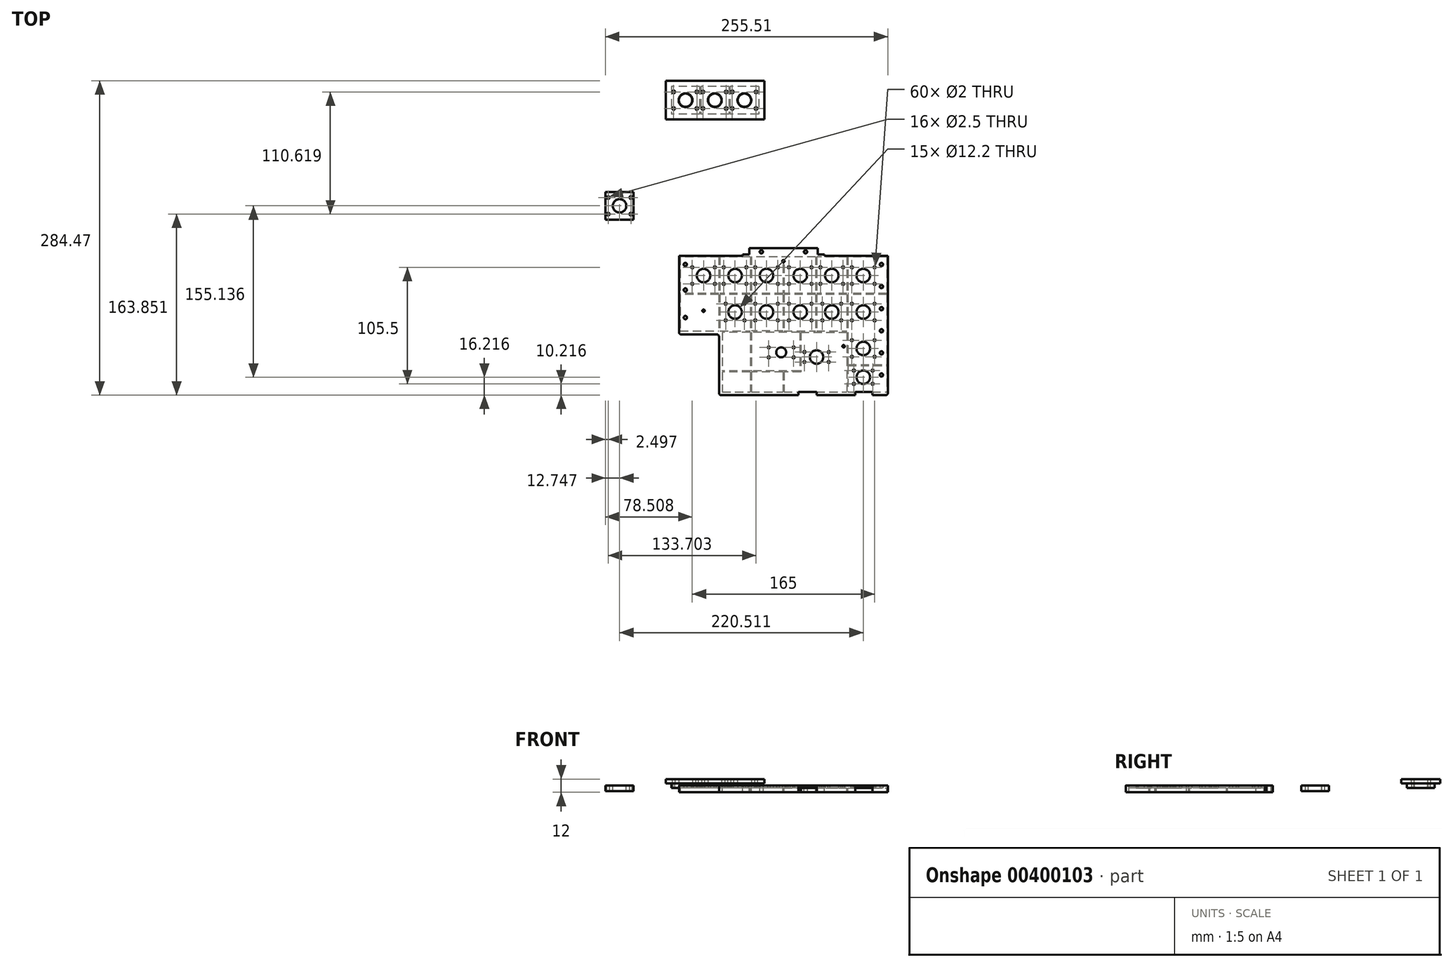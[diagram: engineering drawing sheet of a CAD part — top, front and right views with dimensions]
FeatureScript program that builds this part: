
annotation { "Feature Type Name" : "Feature", "Feature Type Description" : "" }
export const myFeature = defineFeature(function(context is Context, id is Id, definition is map)
    precondition{}
    {
        {
            var Q0;
            Q0=qCreatedBy(makeId("Top.planeOp"),FACE);
            var sketch = newSketch(context, id + "F0", { "sketchPlane" : qUnion([Q0])});
            skLineSegment(sketch, "E0.bottom", {"start": v(7.75, 12.5) * mm, "end": v(-7.75, 12.5) * mm});
            skLineSegment(sketch, "E0.top", {"start": v(7.75, -12.5) * mm, "end": v(-7.75, -12.5) * mm});
            skLineSegment(sketch, "E0.left", {"start": v(7.75, 12.5) * mm, "end": v(7.75, -12.5) * mm});
            skLineSegment(sketch, "E0.right", {"start": v(-7.75, 12.5) * mm, "end": v(-7.75, -12.5) * mm});
            skPoint(sketch, "E0.middle", {"position": v(0, 0) * mm});
            skLineSegment(sketch, "E1.bottom", {"start": v(-7.75, 12.5) * mm, "end": v(-12.75, 12.5) * mm});
            skLineSegment(sketch, "E1.top", {"start": v(-7.75, -12.5) * mm, "end": v(-12.75, -12.5) * mm});
            skLineSegment(sketch, "E1.right", {"start": v(-12.75, 12.5) * mm, "end": v(-12.75, -12.5) * mm});
            skLineSegment(sketch, "E2.bottom", {"start": v(7.75, 12.5) * mm, "end": v(12.75, 12.5) * mm});
            skLineSegment(sketch, "E2.top", {"start": v(7.75, -12.5) * mm, "end": v(12.75, -12.5) * mm});
            skLineSegment(sketch, "E2.right", {"start": v(12.75, 12.5) * mm, "end": v(12.75, -12.5) * mm});
            skCircle(sketch, "E3", {"center": v(-10.75, 7.5) * mm, "radius": 0.9 * mm});
            skPoint(sketch, "E3.centerSnap0", {"position": v(-10.25, 12.5) * mm});
            skCircle(sketch, "E4", {"center": v(-10.75, -7.5) * mm, "radius": 0.9 * mm});
            skCircle(sketch, "E5", {"center": v(10.25, 7.5) * mm, "radius": 0.9 * mm});
            skPoint(sketch, "E5.centerSnap0", {"position": v(10.25, 12.5) * mm});
            skCircle(sketch, "E6", {"center": v(10.25, -7.5) * mm, "radius": 0.9 * mm});
            skCircle(sketch, "E7", {"center": v(0, 0) * mm, "radius": 6 * mm});
            skLineSegment(sketch, "E8.bottom", {"start": v(34.25, 12.5) * mm, "end": v(18.75, 12.5) * mm});
            skLineSegment(sketch, "E8.top", {"start": v(34.25, -12.5) * mm, "end": v(18.75, -12.5) * mm});
            skLineSegment(sketch, "E8.left", {"start": v(34.25, 12.5) * mm, "end": v(34.25, -12.5) * mm});
            skLineSegment(sketch, "E8.right", {"start": v(18.75, 12.5) * mm, "end": v(18.75, -12.5) * mm});
            skPoint(sketch, "E8.middle", {"position": v(26.5, 0) * mm});
            skLineSegment(sketch, "E9.bottom", {"start": v(18.75, 12.5) * mm, "end": v(13.75, 12.5) * mm});
            skLineSegment(sketch, "E9.top", {"start": v(18.75, -12.5) * mm, "end": v(13.75, -12.5) * mm});
            skLineSegment(sketch, "E9.right", {"start": v(13.75, 12.5) * mm, "end": v(13.75, -12.5) * mm});
            skLineSegment(sketch, "E10.bottom", {"start": v(34.25, 12.5) * mm, "end": v(39.25, 12.5) * mm});
            skLineSegment(sketch, "E10.top", {"start": v(34.25, -12.5) * mm, "end": v(39.25, -12.5) * mm});
            skLineSegment(sketch, "E10.right", {"start": v(39.25, 12.5) * mm, "end": v(39.25, -12.5) * mm});
            skCircle(sketch, "E11", {"center": v(15.75, 7.5) * mm, "radius": 0.9 * mm});
            skPoint(sketch, "E11.centerSnap0", {"position": v(16.25, 12.5) * mm});
            skCircle(sketch, "E12", {"center": v(15.75, -7.5) * mm, "radius": 0.9 * mm});
            skCircle(sketch, "E13", {"center": v(36.75, 7.5) * mm, "radius": 0.9 * mm});
            skPoint(sketch, "E13.centerSnap0", {"position": v(36.75, 12.5) * mm});
            skCircle(sketch, "E14", {"center": v(36.75, -7.5) * mm, "radius": 0.9 * mm});
            skCircle(sketch, "E15", {"center": v(26.5, 0) * mm, "radius": 6 * mm});
            skLineSegment(sketch, "E16.bottom", {"start": v(61.25, 12.5) * mm, "end": v(45.25, 12.5) * mm});
            skLineSegment(sketch, "E16.top", {"start": v(61.25, -12.5) * mm, "end": v(45.25, -12.5) * mm});
            skLineSegment(sketch, "E16.left", {"start": v(61.25, 12.5) * mm, "end": v(61.25, -12.5) * mm});
            skLineSegment(sketch, "E16.right", {"start": v(45.25, 12.5) * mm, "end": v(45.25, -12.5) * mm});
            skPoint(sketch, "E16.middle", {"position": v(53.25, 0) * mm});
            skLineSegment(sketch, "E17.bottom", {"start": v(45.25, 12.5) * mm, "end": v(40.25, 12.5) * mm});
            skLineSegment(sketch, "E17.top", {"start": v(45.25, -12.5) * mm, "end": v(40.25, -12.5) * mm});
            skLineSegment(sketch, "E17.right", {"start": v(40.25, 12.5) * mm, "end": v(40.25, -12.5) * mm});
            skLineSegment(sketch, "E18.bottom", {"start": v(61.25, 12.5) * mm, "end": v(66.25, 12.5) * mm});
            skLineSegment(sketch, "E18.top", {"start": v(61.25, -12.5) * mm, "end": v(66.25, -12.5) * mm});
            skLineSegment(sketch, "E18.right", {"start": v(66.25, 12.5) * mm, "end": v(66.25, -12.5) * mm});
            skCircle(sketch, "E19", {"center": v(42.25, 7.5) * mm, "radius": 0.9 * mm});
            skPoint(sketch, "E19.centerSnap0", {"position": v(42.75, 12.5) * mm});
            skCircle(sketch, "E20", {"center": v(42.25, -7.5) * mm, "radius": 0.9 * mm});
            skCircle(sketch, "E21", {"center": v(63.75, 7.5) * mm, "radius": 0.9 * mm});
            skPoint(sketch, "E21.centerSnap0", {"position": v(63.75, 12.5) * mm});
            skCircle(sketch, "E22", {"center": v(63.75, -7.5) * mm, "radius": 0.9 * mm});
            skCircle(sketch, "E23", {"center": v(53.25, 0) * mm, "radius": 6 * mm});
            skSolve(sketch);
        }
        {
            var Q0;
            Q0=makeQuery(id+"F0.imprint","IMPRINT",FACE,{"disambiguationData":[TD([[makeQuery(id+"F0.imprint","IMPRINT",EDGE,{"derivedFrom":sQuery(id+"F0.wireOp",EDGE,"E0.bottom")}),1.0]])]});
            var Q1;
            Q1=makeQuery(id+"F0.imprint","IMPRINT",FACE,{"disambiguationData":[TD([[makeQuery(id+"F0.imprint","IMPRINT",EDGE,{"derivedFrom":sQuery(id+"F0.wireOp",EDGE,"E1.bottom")}),1.0]])]});
            var Q2;
            Q2=makeQuery(id+"F0.imprint","IMPRINT",FACE,{"disambiguationData":[TD([[makeQuery(id+"F0.imprint","IMPRINT",EDGE,{"derivedFrom":sQuery(id+"F0.wireOp",EDGE,"E2.bottom")}),-1.0]])]});
            var Q3;
            Q3=makeQuery(id+"F0.imprint","IMPRINT",FACE,{"disambiguationData":[TD([[makeQuery(id+"F0.imprint","IMPRINT",EDGE,{"derivedFrom":sQuery(id+"F0.wireOp",EDGE,"E9.bottom")}),1.0]])]});
            var Q4;
            Q4=makeQuery(id+"F0.imprint","IMPRINT",FACE,{"disambiguationData":[TD([[makeQuery(id+"F0.imprint","IMPRINT",EDGE,{"derivedFrom":sQuery(id+"F0.wireOp",EDGE,"E8.bottom")}),1.0]])]});
            var Q5;
            Q5=makeQuery(id+"F0.imprint","IMPRINT",FACE,{"disambiguationData":[TD([[makeQuery(id+"F0.imprint","IMPRINT",EDGE,{"derivedFrom":sQuery(id+"F0.wireOp",EDGE,"E10.bottom")}),-1.0]])]});
            var Q6;
            Q6=makeQuery(id+"F0.imprint","IMPRINT",FACE,{"disambiguationData":[TD([[makeQuery(id+"F0.imprint","IMPRINT",EDGE,{"derivedFrom":sQuery(id+"F0.wireOp",EDGE,"E17.bottom")}),1.0]])]});
            var Q7;
            Q7=makeQuery(id+"F0.imprint","IMPRINT",FACE,{"disambiguationData":[TD([[makeQuery(id+"F0.imprint","IMPRINT",EDGE,{"derivedFrom":sQuery(id+"F0.wireOp",EDGE,"E16.bottom")}),1.0]])]});
            var Q8;
            Q8=makeQuery(id+"F0.imprint","IMPRINT",FACE,{"disambiguationData":[TD([[makeQuery(id+"F0.imprint","IMPRINT",EDGE,{"derivedFrom":sQuery(id+"F0.wireOp",EDGE,"E18.bottom")}),-1.0]])]});
            extrude(context, id + "F1", {"entities" : qUnion([Q0, Q1, Q2, Q3, Q4, Q5, Q6, Q7, Q8]), "depth" : 4 * mm});
        }
        {
            var Q0;
            Q0=makeQuery(id+"F1.opExtrude","CAP_FACE",FACE,{"disambiguationData":[OSD([sQuery(id+"F0.wireOp",EDGE,"E0.bottom"),sQuery(id+"F0.wireOp",EDGE,"E0.top"),sQuery(id+"F0.wireOp",EDGE,"E1.bottom"),sQuery(id+"F0.wireOp",EDGE,"E1.top"),sQuery(id+"F0.wireOp",EDGE,"E1.right"),sQuery(id+"F0.wireOp",EDGE,"E2.bottom"),sQuery(id+"F0.wireOp",EDGE,"E2.top"),sQuery(id+"F0.wireOp",EDGE,"E2.right"),sQuery(id+"F0.wireOp",EDGE,"E3"),sQuery(id+"F0.wireOp",EDGE,"E4"),sQuery(id+"F0.wireOp",EDGE,"E5"),sQuery(id+"F0.wireOp",EDGE,"E6"),sQuery(id+"F0.wireOp",EDGE,"E7")])],"isStart":false});
            var sketch = newSketch(context, id + "F2", { "sketchPlane" : qUnion([Q0])});
            skLineSegment(sketch, "E24.bottom", {"start": v(-17.75, 17.5) * mm, "end": v(71.25, 17.5) * mm});
            skLineSegment(sketch, "E24.top", {"start": v(-17.75, -17.5) * mm, "end": v(71.25, -17.5) * mm});
            skLineSegment(sketch, "E24.left", {"start": v(-17.75, 17.5) * mm, "end": v(-17.75, -17.5) * mm});
            skLineSegment(sketch, "E24.right", {"start": v(71.25, 17.5) * mm, "end": v(71.25, -17.5) * mm});
            skCircle(sketch, "E25", {"center": v(-10.75, 7.5) * mm, "radius": 1.25 * mm});
            skCircle(sketch, "E26", {"center": v(-10.75, -7.5) * mm, "radius": 1.25 * mm});
            skCircle(sketch, "E27", {"center": v(10.25, -7.5) * mm, "radius": 1.25 * mm});
            skCircle(sketch, "E28", {"center": v(10.25, 7.5) * mm, "radius": 1.25 * mm});
            skCircle(sketch, "E29", {"center": v(15.75, 7.5) * mm, "radius": 1.25 * mm});
            skCircle(sketch, "E30", {"center": v(15.75, -7.5) * mm, "radius": 1.25 * mm});
            skCircle(sketch, "E31", {"center": v(36.75, -7.5) * mm, "radius": 1.25 * mm});
            skCircle(sketch, "E32", {"center": v(0, 0) * mm, "radius": 6.25 * mm});
            skCircle(sketch, "E33", {"center": v(26.5, 0) * mm, "radius": 6.25 * mm});
            skCircle(sketch, "E34", {"center": v(53.25, 0) * mm, "radius": 6.25 * mm});
            skCircle(sketch, "E35", {"center": v(36.75, 7.5) * mm, "radius": 1.25 * mm});
            skCircle(sketch, "E36", {"center": v(42.25, 7.5) * mm, "radius": 1.25 * mm});
            skCircle(sketch, "E37", {"center": v(42.25, -7.5) * mm, "radius": 1.25 * mm});
            skCircle(sketch, "E38", {"center": v(63.75, 7.5) * mm, "radius": 1.25 * mm});
            skCircle(sketch, "E39", {"center": v(63.75, -7.5) * mm, "radius": 1.25 * mm});
            skSolve(sketch);
        }
        {
            var Q0;
            Q0=qSketchRegion(id+"F2",true);
            extrude(context, id + "F3", {"entities" : qUnion([Q0]), "depth" : 4 * mm});
        }
        {
            var Q0;
            Q0=qCreatedBy(makeId("Top.planeOp"),FACE);
            var sketch = newSketch(context, id + "F4", { "sketchPlane" : qUnion([Q0])});
            skLineSegment(sketch, "E40.bottom", {"start": v(3.56, -143.75) * mm, "end": v(29.06, -143.75) * mm, "construction": true});
            skLineSegment(sketch, "E40.top", {"start": v(3.56, -173.75) * mm, "end": v(29.06, -173.75) * mm, "construction": true});
            skLineSegment(sketch, "E40.left", {"start": v(3.56, -143.75) * mm, "end": v(3.56, -173.75) * mm, "construction": true});
            skLineSegment(sketch, "E40.right", {"start": v(29.06, -143.75) * mm, "end": v(29.06, -173.75) * mm, "construction": true});
            skLineSegment(sketch, "E41.bottom", {"start": v(32.06, -143.75) * mm, "end": v(57.56, -143.75) * mm, "construction": true});
            skLineSegment(sketch, "E41.top", {"start": v(32.06, -173.75) * mm, "end": v(57.56, -173.75) * mm, "construction": true});
            skLineSegment(sketch, "E41.left", {"start": v(32.06, -143.75) * mm, "end": v(32.06, -173.75) * mm, "construction": true});
            skLineSegment(sketch, "E41.right", {"start": v(57.56, -143.75) * mm, "end": v(57.56, -173.75) * mm, "construction": true});
            skLineSegment(sketch, "E42.bottom", {"start": v(60.56, -143.75) * mm, "end": v(86.06, -143.75) * mm, "construction": true});
            skLineSegment(sketch, "E42.top", {"start": v(60.56, -173.75) * mm, "end": v(86.06, -173.75) * mm, "construction": true});
            skLineSegment(sketch, "E42.left", {"start": v(60.56, -143.75) * mm, "end": v(60.56, -173.75) * mm, "construction": true});
            skLineSegment(sketch, "E42.right", {"start": v(86.06, -143.75) * mm, "end": v(86.06, -173.75) * mm, "construction": true});
            skLineSegment(sketch, "E43.bottom", {"start": v(91.06, -143.75) * mm, "end": v(116.56, -143.75) * mm, "construction": true});
            skLineSegment(sketch, "E43.top", {"start": v(91.06, -173.75) * mm, "end": v(116.56, -173.75) * mm, "construction": true});
            skLineSegment(sketch, "E43.left", {"start": v(91.06, -143.75) * mm, "end": v(91.06, -173.75) * mm, "construction": true});
            skLineSegment(sketch, "E43.right", {"start": v(116.56, -143.75) * mm, "end": v(116.56, -173.75) * mm, "construction": true});
            skLineSegment(sketch, "E44.bottom", {"start": v(119.56, -143.75) * mm, "end": v(145.06, -143.75) * mm, "construction": true});
            skLineSegment(sketch, "E44.top", {"start": v(119.56, -173.75) * mm, "end": v(145.06, -173.75) * mm, "construction": true});
            skLineSegment(sketch, "E44.left", {"start": v(119.56, -143.75) * mm, "end": v(119.56, -173.75) * mm, "construction": true});
            skLineSegment(sketch, "E44.right", {"start": v(145.06, -143.75) * mm, "end": v(145.06, -173.75) * mm, "construction": true});
            skLineSegment(sketch, "E45.bottom", {"start": v(148.06, -143.75) * mm, "end": v(173.56, -143.75) * mm, "construction": true});
            skLineSegment(sketch, "E45.top", {"start": v(148.06, -173.75) * mm, "end": v(173.56, -173.75) * mm, "construction": true});
            skLineSegment(sketch, "E45.left", {"start": v(148.06, -143.75) * mm, "end": v(148.06, -173.75) * mm, "construction": true});
            skLineSegment(sketch, "E45.right", {"start": v(173.56, -143.75) * mm, "end": v(173.56, -173.75) * mm, "construction": true});
            skLineSegment(sketch, "E46.bottom", {"start": v(60.56, -176.75) * mm, "end": v(86.06, -176.75) * mm, "construction": true});
            skLineSegment(sketch, "E46.top", {"start": v(60.56, -206.75) * mm, "end": v(86.06, -206.75) * mm, "construction": true});
            skLineSegment(sketch, "E46.left", {"start": v(60.56, -176.75) * mm, "end": v(60.56, -206.75) * mm, "construction": true});
            skLineSegment(sketch, "E46.right", {"start": v(86.06, -176.75) * mm, "end": v(86.06, -206.75) * mm, "construction": true});
            skLineSegment(sketch, "E47.bottom", {"start": v(91.06, -176.75) * mm, "end": v(116.56, -176.75) * mm, "construction": true});
            skLineSegment(sketch, "E47.top", {"start": v(91.06, -206.75) * mm, "end": v(116.56, -206.75) * mm, "construction": true});
            skLineSegment(sketch, "E47.left", {"start": v(91.06, -176.75) * mm, "end": v(91.06, -206.75) * mm, "construction": true});
            skLineSegment(sketch, "E47.right", {"start": v(116.56, -176.75) * mm, "end": v(116.56, -206.75) * mm, "construction": true});
            skLineSegment(sketch, "E48.bottom", {"start": v(148.06, -176.75) * mm, "end": v(173.56, -176.75) * mm, "construction": true});
            skLineSegment(sketch, "E48.top", {"start": v(148.06, -206.75) * mm, "end": v(173.56, -206.75) * mm, "construction": true});
            skLineSegment(sketch, "E48.left", {"start": v(148.06, -176.75) * mm, "end": v(148.06, -206.75) * mm, "construction": true});
            skLineSegment(sketch, "E48.right", {"start": v(173.56, -176.75) * mm, "end": v(173.56, -206.75) * mm, "construction": true});
            skLineSegment(sketch, "E49.bottom", {"start": v(148.06, -208.75) * mm, "end": v(173.56, -208.75) * mm, "construction": true});
            skLineSegment(sketch, "E49.top", {"start": v(148.06, -238.75) * mm, "end": v(173.56, -238.75) * mm, "construction": true});
            skLineSegment(sketch, "E49.left", {"start": v(148.06, -208.75) * mm, "end": v(148.06, -238.75) * mm, "construction": true});
            skLineSegment(sketch, "E49.right", {"start": v(173.56, -208.75) * mm, "end": v(173.56, -238.75) * mm, "construction": true});
            skLineSegment(sketch, "E50.bottom", {"start": v(-4.94, -140.75) * mm, "end": v(182.06, -140.75) * mm});
            skLineSegment(sketch, "E50.top", {"start": v(33.28, -263.97) * mm, "end": v(182.06, -263.97) * mm});
            skLineSegment(sketch, "E50.left", {"start": v(-4.94, -140.75) * mm, "end": v(-4.94, -208.97) * mm});
            skLineSegment(sketch, "E50.right", {"start": v(182.06, -140.75) * mm, "end": v(182.06, -263.97) * mm});
            skLineSegment(sketch, "E51", {"start": v(-4.94, -208.97) * mm, "end": v(33.28, -208.97) * mm});
            skLineSegment(sketch, "E52", {"start": v(33.28, -208.97) * mm, "end": v(33.28, -263.97) * mm});
            skLineSegment(sketch, "E53.bottom", {"start": v(-67.45, -83.12) * mm, "end": v(-51.95, -83.12) * mm});
            skLineSegment(sketch, "E53.top", {"start": v(-67.45, -108.12) * mm, "end": v(-51.95, -108.12) * mm});
            skLineSegment(sketch, "E53.left", {"start": v(-67.45, -83.12) * mm, "end": v(-67.45, -108.12) * mm});
            skLineSegment(sketch, "E53.right", {"start": v(-51.95, -83.12) * mm, "end": v(-51.95, -108.12) * mm});
            skLineSegment(sketch, "E54.bottom", {"start": v(-51.95, -83.12) * mm, "end": v(-46.95, -83.12) * mm});
            skLineSegment(sketch, "E54.top", {"start": v(-51.95, -108.12) * mm, "end": v(-46.95, -108.12) * mm});
            skLineSegment(sketch, "E54.right", {"start": v(-46.95, -83.12) * mm, "end": v(-46.95, -108.12) * mm});
            skLineSegment(sketch, "E55.bottom", {"start": v(-67.45, -83.12) * mm, "end": v(-72.45, -83.12) * mm});
            skLineSegment(sketch, "E55.top", {"start": v(-67.45, -108.12) * mm, "end": v(-72.45, -108.12) * mm});
            skLineSegment(sketch, "E55.right", {"start": v(-72.45, -83.12) * mm, "end": v(-72.45, -108.12) * mm});
            skCircle(sketch, "E56", {"center": v(-59.7, -95.62) * mm, "radius": 6.1 * mm});
            skPoint(sketch, "E56.centerSnap0", {"position": v(-67.45, -95.62) * mm});
            skPoint(sketch, "E56.centerSnap1", {"position": v(-59.7, -83.12) * mm});
            skCircle(sketch, "E57", {"center": v(-69.95, -88.12) * mm, "radius": 1.25 * mm});
            skPoint(sketch, "E57.centerSnap0", {"position": v(-69.95, -83.12) * mm});
            skCircle(sketch, "E58", {"center": v(-69.95, -103.12) * mm, "radius": 1.25 * mm});
            skCircle(sketch, "E59", {"center": v(-49.45, -88.12) * mm, "radius": 1.25 * mm});
            skPoint(sketch, "E59.centerSnap0", {"position": v(-49.45, -83.12) * mm});
            skCircle(sketch, "E60", {"center": v(-49.45, -103.12) * mm, "radius": 1.25 * mm});
            skLineSegment(sketch, "E61.bottom", {"start": v(33.8, -180.75) * mm, "end": v(55.8, -180.75) * mm, "construction": true});
            skLineSegment(sketch, "E61.top", {"start": v(33.8, -202.75) * mm, "end": v(55.8, -202.75) * mm, "construction": true});
            skLineSegment(sketch, "E61.left", {"start": v(33.8, -180.75) * mm, "end": v(33.8, -202.75) * mm, "construction": true});
            skLineSegment(sketch, "E61.right", {"start": v(55.8, -180.75) * mm, "end": v(55.8, -202.75) * mm, "construction": true});
            skLineSegment(sketch, "E62.bottom", {"start": v(121.3, -180.75) * mm, "end": v(143.3, -180.75) * mm, "construction": true});
            skLineSegment(sketch, "E62.top", {"start": v(121.3, -202.75) * mm, "end": v(143.3, -202.75) * mm, "construction": true});
            skLineSegment(sketch, "E62.left", {"start": v(121.3, -180.75) * mm, "end": v(121.3, -202.75) * mm, "construction": true});
            skLineSegment(sketch, "E62.right", {"start": v(143.3, -180.75) * mm, "end": v(143.3, -202.75) * mm, "construction": true});
            skLineSegment(sketch, "E63.bottom", {"start": v(105.06, -224.97) * mm, "end": v(111.06, -224.97) * mm, "construction": true});
            skLineSegment(sketch, "E63.top", {"start": v(105.06, -239.97) * mm, "end": v(110.06, -239.97) * mm, "construction": true});
            skLineSegment(sketch, "E63.left", {"start": v(105.06, -224.97) * mm, "end": v(105.06, -239.97) * mm, "construction": true});
            skLineSegment(sketch, "E64.bottom", {"start": v(132.06, -224.97) * mm, "end": v(126.06, -224.97) * mm, "construction": true});
            skLineSegment(sketch, "E64.top", {"start": v(132.06, -239.97) * mm, "end": v(126.06, -239.97) * mm, "construction": true});
            skLineSegment(sketch, "E64.left", {"start": v(132.06, -224.97) * mm, "end": v(132.06, -239.97) * mm, "construction": true});
            skLineSegment(sketch, "E64.right", {"start": v(126.06, -224.97) * mm, "end": v(126.06, -239.97) * mm, "construction": true});
            skLineSegment(sketch, "E65.bottom", {"start": v(3.56, -146.25) * mm, "end": v(8.56, -146.25) * mm, "construction": true});
            skLineSegment(sketch, "E65.top", {"start": v(3.56, -171.25) * mm, "end": v(8.56, -171.25) * mm, "construction": true});
            skLineSegment(sketch, "E65.left", {"start": v(3.56, -146.25) * mm, "end": v(3.56, -171.25) * mm, "construction": true});
            skLineSegment(sketch, "E65.right", {"start": v(8.56, -146.25) * mm, "end": v(8.56, -171.25) * mm, "construction": true});
            skLineSegment(sketch, "E66.bottom", {"start": v(29.06, -146.25) * mm, "end": v(24.06, -146.25) * mm, "construction": true});
            skLineSegment(sketch, "E66.top", {"start": v(29.06, -171.25) * mm, "end": v(24.06, -171.25) * mm, "construction": true});
            skLineSegment(sketch, "E66.left", {"start": v(29.06, -146.25) * mm, "end": v(29.06, -171.25) * mm, "construction": true});
            skLineSegment(sketch, "E66.right", {"start": v(24.06, -146.25) * mm, "end": v(24.06, -171.25) * mm, "construction": true});
            skCircle(sketch, "E67", {"center": v(6.06, -151.25) * mm, "radius": 1 * mm});
            skPoint(sketch, "E67.centerSnap0", {"position": v(6.06, -146.25) * mm});
            skCircle(sketch, "E68", {"center": v(6.06, -166.25) * mm, "radius": 1 * mm});
            skCircle(sketch, "E69", {"center": v(16.3, -158.75) * mm, "radius": 6.1 * mm});
            skPoint(sketch, "E69.centerSnap0", {"position": v(8.56, -158.75) * mm});
            skPoint(sketch, "E69.centerSnap1", {"position": v(16.3, -143.75) * mm});
            skCircle(sketch, "E70", {"center": v(26.56, -151.25) * mm, "radius": 1 * mm});
            skPoint(sketch, "E70.centerSnap0", {"position": v(26.56, -146.25) * mm});
            skCircle(sketch, "E71", {"center": v(26.56, -166.25) * mm, "radius": 1 * mm});
            skCircle(sketch, "E72", {"center": v(107.56, -227.97) * mm, "radius": 1 * mm});
            skPoint(sketch, "E72.centerSnap0", {"position": v(108.06, -224.97) * mm});
            skCircle(sketch, "E73", {"center": v(107.56, -236.97) * mm, "radius": 1 * mm});
            skPoint(sketch, "E73.centerSnap0", {"position": v(107.56, -239.97) * mm});
            skCircle(sketch, "E74", {"center": v(129.56, -227.97) * mm, "radius": 1 * mm});
            skPoint(sketch, "E74.centerSnap0", {"position": v(129.06, -224.97) * mm});
            skCircle(sketch, "E75", {"center": v(129.56, -236.97) * mm, "radius": 1 * mm});
            skPoint(sketch, "E75.centerSnap0", {"position": v(129.06, -239.97) * mm});
            skPoint(sketch, "E76.centerSnap0", {"position": v(110.56, -232.47) * mm});
            skLineSegment(sketch, "E77.bottom", {"start": v(38.8, -185.75) * mm, "end": v(50.8, -185.75) * mm, "construction": true});
            skLineSegment(sketch, "E77.top", {"start": v(38.8, -197.75) * mm, "end": v(50.8, -197.75) * mm, "construction": true});
            skLineSegment(sketch, "E77.left", {"start": v(38.8, -185.75) * mm, "end": v(38.8, -197.75) * mm, "construction": true});
            skLineSegment(sketch, "E77.right", {"start": v(50.8, -185.75) * mm, "end": v(50.8, -197.75) * mm, "construction": true});
            skLineSegment(sketch, "E78.bottom", {"start": v(149.8, -239.75) * mm, "end": v(171.8, -239.75) * mm, "construction": true});
            skLineSegment(sketch, "E78.top", {"start": v(149.8, -261.75) * mm, "end": v(171.8, -261.75) * mm, "construction": true});
            skLineSegment(sketch, "E78.left", {"start": v(149.8, -239.75) * mm, "end": v(149.8, -261.75) * mm, "construction": true});
            skLineSegment(sketch, "E78.right", {"start": v(171.8, -239.75) * mm, "end": v(171.8, -261.75) * mm, "construction": true});
            skLineSegment(sketch, "E79.bottom", {"start": v(154.8, -244.75) * mm, "end": v(166.8, -244.75) * mm, "construction": true});
            skLineSegment(sketch, "E79.top", {"start": v(154.8, -256.75) * mm, "end": v(166.8, -256.75) * mm, "construction": true});
            skLineSegment(sketch, "E79.left", {"start": v(154.8, -244.75) * mm, "end": v(154.8, -256.75) * mm, "construction": true});
            skLineSegment(sketch, "E79.right", {"start": v(166.8, -244.75) * mm, "end": v(166.8, -256.75) * mm, "construction": true});
            skLineSegment(sketch, "E80.bottom", {"start": v(77.8, -218.75) * mm, "end": v(95.3, -218.75) * mm, "construction": true});
            skLineSegment(sketch, "E80.top", {"start": v(77.8, -237.75) * mm, "end": v(95.3, -237.75) * mm, "construction": true});
            skLineSegment(sketch, "E80.left", {"start": v(77.8, -218.75) * mm, "end": v(77.8, -237.75) * mm, "construction": true});
            skLineSegment(sketch, "E80.right", {"start": v(95.3, -218.75) * mm, "end": v(95.3, -237.75) * mm, "construction": true});
            skLineSegment(sketch, "E81.bottom", {"start": v(32.06, -146.25) * mm, "end": v(37.06, -146.25) * mm, "construction": true});
            skLineSegment(sketch, "E81.top", {"start": v(32.06, -171.25) * mm, "end": v(37.06, -171.25) * mm, "construction": true});
            skLineSegment(sketch, "E81.left", {"start": v(32.06, -146.25) * mm, "end": v(32.06, -171.25) * mm, "construction": true});
            skLineSegment(sketch, "E81.right", {"start": v(37.06, -146.25) * mm, "end": v(37.06, -171.25) * mm, "construction": true});
            skLineSegment(sketch, "E82.bottom", {"start": v(57.56, -146.25) * mm, "end": v(52.56, -146.25) * mm, "construction": true});
            skLineSegment(sketch, "E82.top", {"start": v(57.56, -171.25) * mm, "end": v(52.56, -171.25) * mm, "construction": true});
            skLineSegment(sketch, "E82.left", {"start": v(57.56, -146.25) * mm, "end": v(57.56, -171.25) * mm, "construction": true});
            skLineSegment(sketch, "E82.right", {"start": v(52.56, -146.25) * mm, "end": v(52.56, -171.25) * mm, "construction": true});
            skCircle(sketch, "E83", {"center": v(34.56, -151.25) * mm, "radius": 1 * mm});
            skPoint(sketch, "E83.centerSnap0", {"position": v(34.56, -146.25) * mm});
            skCircle(sketch, "E84", {"center": v(34.56, -166.25) * mm, "radius": 1 * mm});
            skCircle(sketch, "E85", {"center": v(55.06, -151.25) * mm, "radius": 1 * mm});
            skPoint(sketch, "E85.centerSnap0", {"position": v(55.06, -146.25) * mm});
            skCircle(sketch, "E86", {"center": v(55.06, -166.25) * mm, "radius": 1 * mm});
            skCircle(sketch, "E87", {"center": v(44.8, -158.75) * mm, "radius": 6.1 * mm});
            skPoint(sketch, "E87.centerSnap0", {"position": v(37.06, -158.75) * mm});
            skPoint(sketch, "E87.centerSnap1", {"position": v(44.8, -143.75) * mm});
            skLineSegment(sketch, "E88.bottom", {"start": v(60.56, -146.25) * mm, "end": v(65.56, -146.25) * mm, "construction": true});
            skLineSegment(sketch, "E88.top", {"start": v(60.56, -171.25) * mm, "end": v(65.56, -171.25) * mm, "construction": true});
            skLineSegment(sketch, "E88.left", {"start": v(60.56, -146.25) * mm, "end": v(60.56, -171.25) * mm, "construction": true});
            skLineSegment(sketch, "E88.right", {"start": v(65.56, -146.25) * mm, "end": v(65.56, -171.25) * mm, "construction": true});
            skLineSegment(sketch, "E89.bottom", {"start": v(86.06, -146.25) * mm, "end": v(81.06, -146.25) * mm, "construction": true});
            skLineSegment(sketch, "E89.top", {"start": v(86.06, -171.25) * mm, "end": v(81.06, -171.25) * mm, "construction": true});
            skLineSegment(sketch, "E89.left", {"start": v(86.06, -146.25) * mm, "end": v(86.06, -171.25) * mm, "construction": true});
            skLineSegment(sketch, "E89.right", {"start": v(81.06, -146.25) * mm, "end": v(81.06, -171.25) * mm, "construction": true});
            skLineSegment(sketch, "E90.bottom", {"start": v(91.06, -146.25) * mm, "end": v(96.06, -146.25) * mm, "construction": true});
            skLineSegment(sketch, "E90.top", {"start": v(91.06, -171.25) * mm, "end": v(96.06, -171.25) * mm, "construction": true});
            skLineSegment(sketch, "E90.left", {"start": v(91.06, -146.25) * mm, "end": v(91.06, -171.25) * mm, "construction": true});
            skLineSegment(sketch, "E90.right", {"start": v(96.06, -146.25) * mm, "end": v(96.06, -171.25) * mm, "construction": true});
            skLineSegment(sketch, "E91.bottom", {"start": v(116.56, -146.25) * mm, "end": v(111.56, -146.25) * mm, "construction": true});
            skLineSegment(sketch, "E91.top", {"start": v(116.56, -171.25) * mm, "end": v(111.56, -171.25) * mm, "construction": true});
            skLineSegment(sketch, "E91.left", {"start": v(116.56, -146.25) * mm, "end": v(116.56, -171.25) * mm, "construction": true});
            skLineSegment(sketch, "E91.right", {"start": v(111.56, -146.25) * mm, "end": v(111.56, -171.25) * mm, "construction": true});
            skLineSegment(sketch, "E92.bottom", {"start": v(119.56, -146.25) * mm, "end": v(124.56, -146.25) * mm, "construction": true});
            skLineSegment(sketch, "E92.top", {"start": v(119.56, -171.25) * mm, "end": v(124.56, -171.25) * mm, "construction": true});
            skLineSegment(sketch, "E92.left", {"start": v(119.56, -146.25) * mm, "end": v(119.56, -171.25) * mm, "construction": true});
            skLineSegment(sketch, "E92.right", {"start": v(124.56, -146.25) * mm, "end": v(124.56, -171.25) * mm, "construction": true});
            skLineSegment(sketch, "E93.bottom", {"start": v(145.06, -146.25) * mm, "end": v(140.06, -146.25) * mm, "construction": true});
            skLineSegment(sketch, "E93.top", {"start": v(145.06, -171.25) * mm, "end": v(140.06, -171.25) * mm, "construction": true});
            skLineSegment(sketch, "E93.left", {"start": v(145.06, -146.25) * mm, "end": v(145.06, -171.25) * mm, "construction": true});
            skLineSegment(sketch, "E93.right", {"start": v(140.06, -146.25) * mm, "end": v(140.06, -171.25) * mm, "construction": true});
            skLineSegment(sketch, "E94.bottom", {"start": v(148.06, -146.25) * mm, "end": v(153.06, -146.25) * mm, "construction": true});
            skLineSegment(sketch, "E94.top", {"start": v(148.06, -171.25) * mm, "end": v(153.06, -171.25) * mm, "construction": true});
            skLineSegment(sketch, "E94.left", {"start": v(148.06, -146.25) * mm, "end": v(148.06, -171.25) * mm, "construction": true});
            skLineSegment(sketch, "E94.right", {"start": v(153.06, -146.25) * mm, "end": v(153.06, -171.25) * mm, "construction": true});
            skLineSegment(sketch, "E95.bottom", {"start": v(173.56, -146.25) * mm, "end": v(168.56, -146.25) * mm, "construction": true});
            skLineSegment(sketch, "E95.top", {"start": v(173.56, -171.25) * mm, "end": v(168.56, -171.25) * mm, "construction": true});
            skLineSegment(sketch, "E95.left", {"start": v(173.56, -146.25) * mm, "end": v(173.56, -171.25) * mm, "construction": true});
            skLineSegment(sketch, "E95.right", {"start": v(168.56, -146.25) * mm, "end": v(168.56, -171.25) * mm, "construction": true});
            skLineSegment(sketch, "E96.bottom", {"start": v(60.56, -179.25) * mm, "end": v(65.56, -179.25) * mm, "construction": true});
            skLineSegment(sketch, "E96.top", {"start": v(60.56, -204.25) * mm, "end": v(65.56, -204.25) * mm, "construction": true});
            skLineSegment(sketch, "E96.left", {"start": v(60.56, -179.25) * mm, "end": v(60.56, -204.25) * mm, "construction": true});
            skLineSegment(sketch, "E96.right", {"start": v(65.56, -179.25) * mm, "end": v(65.56, -204.25) * mm, "construction": true});
            skLineSegment(sketch, "E97.bottom", {"start": v(86.06, -179.25) * mm, "end": v(81.06, -179.25) * mm, "construction": true});
            skLineSegment(sketch, "E97.top", {"start": v(86.06, -204.25) * mm, "end": v(81.06, -204.25) * mm, "construction": true});
            skLineSegment(sketch, "E97.left", {"start": v(86.06, -179.25) * mm, "end": v(86.06, -204.25) * mm, "construction": true});
            skLineSegment(sketch, "E97.right", {"start": v(81.06, -179.25) * mm, "end": v(81.06, -204.25) * mm, "construction": true});
            skLineSegment(sketch, "E98.bottom", {"start": v(91.06, -179.25) * mm, "end": v(96.06, -179.25) * mm, "construction": true});
            skLineSegment(sketch, "E98.top", {"start": v(91.06, -204.25) * mm, "end": v(96.06, -204.25) * mm, "construction": true});
            skLineSegment(sketch, "E98.left", {"start": v(91.06, -179.25) * mm, "end": v(91.06, -204.25) * mm, "construction": true});
            skLineSegment(sketch, "E98.right", {"start": v(96.06, -179.25) * mm, "end": v(96.06, -204.25) * mm, "construction": true});
            skLineSegment(sketch, "E99.bottom", {"start": v(116.56, -179.25) * mm, "end": v(111.56, -179.25) * mm, "construction": true});
            skLineSegment(sketch, "E99.top", {"start": v(116.56, -204.25) * mm, "end": v(111.56, -204.25) * mm, "construction": true});
            skLineSegment(sketch, "E99.left", {"start": v(116.56, -179.25) * mm, "end": v(116.56, -204.25) * mm, "construction": true});
            skLineSegment(sketch, "E99.right", {"start": v(111.56, -179.25) * mm, "end": v(111.56, -204.25) * mm, "construction": true});
            skLineSegment(sketch, "E100.bottom", {"start": v(148.06, -179.25) * mm, "end": v(153.06, -179.25) * mm, "construction": true});
            skLineSegment(sketch, "E100.top", {"start": v(148.06, -204.25) * mm, "end": v(153.06, -204.25) * mm, "construction": true});
            skLineSegment(sketch, "E100.left", {"start": v(148.06, -179.25) * mm, "end": v(148.06, -204.25) * mm, "construction": true});
            skLineSegment(sketch, "E100.right", {"start": v(153.06, -179.25) * mm, "end": v(153.06, -204.25) * mm, "construction": true});
            skLineSegment(sketch, "E101.bottom", {"start": v(173.56, -179.25) * mm, "end": v(168.56, -179.25) * mm, "construction": true});
            skLineSegment(sketch, "E101.top", {"start": v(173.56, -204.25) * mm, "end": v(168.56, -204.25) * mm, "construction": true});
            skLineSegment(sketch, "E101.left", {"start": v(173.56, -179.25) * mm, "end": v(173.56, -204.25) * mm, "construction": true});
            skLineSegment(sketch, "E101.right", {"start": v(168.56, -179.25) * mm, "end": v(168.56, -204.25) * mm, "construction": true});
            skLineSegment(sketch, "E102.bottom", {"start": v(148.06, -212.25) * mm, "end": v(153.06, -212.25) * mm, "construction": true});
            skLineSegment(sketch, "E102.top", {"start": v(148.06, -237.25) * mm, "end": v(153.06, -237.25) * mm, "construction": true});
            skLineSegment(sketch, "E102.left", {"start": v(148.06, -212.25) * mm, "end": v(148.06, -237.25) * mm, "construction": true});
            skLineSegment(sketch, "E102.right", {"start": v(153.06, -212.25) * mm, "end": v(153.06, -237.25) * mm, "construction": true});
            skLineSegment(sketch, "E103.bottom", {"start": v(173.56, -212.25) * mm, "end": v(168.56, -212.25) * mm, "construction": true});
            skLineSegment(sketch, "E103.top", {"start": v(173.56, -237.25) * mm, "end": v(168.56, -237.25) * mm, "construction": true});
            skLineSegment(sketch, "E103.left", {"start": v(173.56, -212.25) * mm, "end": v(173.56, -237.25) * mm, "construction": true});
            skLineSegment(sketch, "E103.right", {"start": v(168.56, -212.25) * mm, "end": v(168.56, -237.25) * mm, "construction": true});
            skCircle(sketch, "E104", {"center": v(63.06, -151.25) * mm, "radius": 1 * mm});
            skPoint(sketch, "E104.centerSnap0", {"position": v(63.06, -146.25) * mm});
            skCircle(sketch, "E105", {"center": v(63.06, -166.25) * mm, "radius": 1 * mm});
            skCircle(sketch, "E106", {"center": v(83.56, -151.25) * mm, "radius": 1 * mm});
            skPoint(sketch, "E106.centerSnap0", {"position": v(83.56, -146.25) * mm});
            skCircle(sketch, "E107", {"center": v(83.56, -166.25) * mm, "radius": 1 * mm});
            skCircle(sketch, "E108", {"center": v(73.3, -158.75) * mm, "radius": 6.1 * mm});
            skPoint(sketch, "E108.centerSnap0", {"position": v(73.3, -143.75) * mm});
            skCircle(sketch, "E109", {"center": v(63.06, -184.25) * mm, "radius": 1 * mm});
            skPoint(sketch, "E109.centerSnap0", {"position": v(63.06, -179.25) * mm});
            skCircle(sketch, "E110", {"center": v(63.06, -199.25) * mm, "radius": 1 * mm});
            skCircle(sketch, "E111", {"center": v(83.56, -184.25) * mm, "radius": 1 * mm});
            skPoint(sketch, "E111.centerSnap0", {"position": v(83.56, -179.25) * mm});
            skCircle(sketch, "E112", {"center": v(83.56, -199.25) * mm, "radius": 1 * mm});
            skCircle(sketch, "E113", {"center": v(73.3, -191.75) * mm, "radius": 6.1 * mm});
            skPoint(sketch, "E113.centerSnap0", {"position": v(65.56, -191.75) * mm});
            skPoint(sketch, "E113.centerSnap1", {"position": v(73.3, -176.75) * mm});
            skLineSegment(sketch, "E114.bottom", {"start": v(77.8, -218.75) * mm, "end": v(72.8, -218.75) * mm, "construction": true});
            skLineSegment(sketch, "E114.top", {"start": v(77.8, -237.75) * mm, "end": v(72.8, -237.75) * mm, "construction": true});
            skLineSegment(sketch, "E114.right", {"start": v(72.8, -218.75) * mm, "end": v(72.8, -237.75) * mm, "construction": true});
            skLineSegment(sketch, "E115.bottom", {"start": v(95.3, -218.75) * mm, "end": v(100.3, -218.75) * mm, "construction": true});
            skLineSegment(sketch, "E115.top", {"start": v(95.3, -237.75) * mm, "end": v(100.3, -237.75) * mm, "construction": true});
            skLineSegment(sketch, "E115.right", {"start": v(100.3, -218.75) * mm, "end": v(100.3, -237.75) * mm, "construction": true});
            skCircle(sketch, "E116", {"center": v(86.56, -228.25) * mm, "radius": 4.5 * mm});
            skPoint(sketch, "E116.centerSnap0", {"position": v(86.56, -218.75) * mm});
            skPoint(sketch, "E116.centerSnap1", {"position": v(77.8, -228.25) * mm});
            skLineSegment(sketch, "E117.bottom", {"start": v(126.3, -185.75) * mm, "end": v(138.3, -185.75) * mm, "construction": true});
            skLineSegment(sketch, "E117.top", {"start": v(126.3, -197.75) * mm, "end": v(138.3, -197.75) * mm, "construction": true});
            skLineSegment(sketch, "E117.left", {"start": v(126.3, -185.75) * mm, "end": v(126.3, -197.75) * mm, "construction": true});
            skLineSegment(sketch, "E117.right", {"start": v(138.3, -185.75) * mm, "end": v(138.3, -197.75) * mm, "construction": true});
            skCircle(sketch, "E118", {"center": v(75.3, -223.75) * mm, "radius": 1 * mm});
            skPoint(sketch, "E118.centerSnap0", {"position": v(75.3, -218.75) * mm});
            skCircle(sketch, "E119", {"center": v(75.3, -232.75) * mm, "radius": 1 * mm});
            skCircle(sketch, "E120", {"center": v(97.8, -223.75) * mm, "radius": 1 * mm});
            skPoint(sketch, "E120.centerSnap0", {"position": v(97.8, -218.75) * mm});
            skCircle(sketch, "E121", {"center": v(97.8, -232.75) * mm, "radius": 1 * mm});
            skCircle(sketch, "E122", {"center": v(93.56, -151.25) * mm, "radius": 1 * mm});
            skPoint(sketch, "E122.centerSnap0", {"position": v(93.56, -146.25) * mm});
            skCircle(sketch, "E123", {"center": v(93.56, -166.25) * mm, "radius": 1 * mm});
            skCircle(sketch, "E124", {"center": v(103.8, -158.75) * mm, "radius": 6.1 * mm});
            skPoint(sketch, "E124.centerSnap0", {"position": v(103.8, -143.75) * mm});
            skCircle(sketch, "E125", {"center": v(114.06, -151.25) * mm, "radius": 1 * mm});
            skPoint(sketch, "E125.centerSnap0", {"position": v(114.06, -146.25) * mm});
            skCircle(sketch, "E126", {"center": v(114.06, -166.25) * mm, "radius": 1 * mm});
            skCircle(sketch, "E127", {"center": v(93.56, -184.25) * mm, "radius": 1 * mm});
            skPoint(sketch, "E127.centerSnap0", {"position": v(93.56, -179.25) * mm});
            skCircle(sketch, "E128", {"center": v(93.56, -199.25) * mm, "radius": 1 * mm});
            skCircle(sketch, "E129", {"center": v(114.06, -184.25) * mm, "radius": 1 * mm});
            skPoint(sketch, "E129.centerSnap0", {"position": v(114.06, -179.25) * mm});
            skCircle(sketch, "E130", {"center": v(114.06, -199.25) * mm, "radius": 1 * mm});
            skCircle(sketch, "E131", {"center": v(103.8, -191.75) * mm, "radius": 6.1 * mm});
            skPoint(sketch, "E131.centerSnap0", {"position": v(96.06, -191.75) * mm});
            skPoint(sketch, "E131.centerSnap1", {"position": v(103.8, -176.75) * mm});
            skCircle(sketch, "E132", {"center": v(122.06, -151.25) * mm, "radius": 1 * mm});
            skPoint(sketch, "E132.centerSnap0", {"position": v(122.06, -146.25) * mm});
            skCircle(sketch, "E133", {"center": v(122.06, -166.25) * mm, "radius": 1 * mm});
            skCircle(sketch, "E134", {"center": v(132.3, -158.75) * mm, "radius": 6.1 * mm});
            skPoint(sketch, "E134.centerSnap0", {"position": v(124.56, -158.75) * mm});
            skPoint(sketch, "E134.centerSnap1", {"position": v(132.3, -143.75) * mm});
            skCircle(sketch, "E135", {"center": v(142.56, -151.25) * mm, "radius": 1 * mm});
            skPoint(sketch, "E135.centerSnap0", {"position": v(142.56, -146.25) * mm});
            skCircle(sketch, "E136", {"center": v(142.56, -166.25) * mm, "radius": 1 * mm});
            skCircle(sketch, "E137", {"center": v(150.56, -151.25) * mm, "radius": 1 * mm});
            skPoint(sketch, "E137.centerSnap0", {"position": v(150.56, -146.25) * mm});
            skCircle(sketch, "E138", {"center": v(150.56, -166.25) * mm, "radius": 1 * mm});
            skCircle(sketch, "E139", {"center": v(171.06, -151.25) * mm, "radius": 1 * mm});
            skPoint(sketch, "E139.centerSnap0", {"position": v(171.06, -146.25) * mm});
            skCircle(sketch, "E140", {"center": v(171.06, -166.25) * mm, "radius": 1 * mm});
            skCircle(sketch, "E141", {"center": v(160.8, -158.75) * mm, "radius": 6.1 * mm});
            skPoint(sketch, "E141.centerSnap0", {"position": v(153.06, -158.75) * mm});
            skPoint(sketch, "E141.centerSnap1", {"position": v(160.8, -143.75) * mm});
            skCircle(sketch, "E142", {"center": v(150.56, -184.25) * mm, "radius": 1 * mm});
            skPoint(sketch, "E142.centerSnap0", {"position": v(150.56, -179.25) * mm});
            skCircle(sketch, "E143", {"center": v(150.56, -199.25) * mm, "radius": 1 * mm});
            skCircle(sketch, "E144", {"center": v(171.06, -184.25) * mm, "radius": 1 * mm});
            skPoint(sketch, "E144.centerSnap0", {"position": v(171.06, -179.25) * mm});
            skCircle(sketch, "E145", {"center": v(171.06, -199.25) * mm, "radius": 1 * mm});
            skCircle(sketch, "E146", {"center": v(160.8, -191.75) * mm, "radius": 6.1 * mm});
            skPoint(sketch, "E146.centerSnap0", {"position": v(153.06, -191.75) * mm});
            skPoint(sketch, "E146.centerSnap1", {"position": v(160.8, -176.75) * mm});
            skCircle(sketch, "E147", {"center": v(16.3, -190.57) * mm, "radius": 1.1 * mm});
            skCircle(sketch, "E148", {"center": v(143.06, -222.72) * mm, "radius": 1.1 * mm});
            skCircle(sketch, "E149", {"center": v(150.56, -217.25) * mm, "radius": 1 * mm});
            skPoint(sketch, "E149.centerSnap0", {"position": v(150.56, -212.25) * mm});
            skCircle(sketch, "E150", {"center": v(150.56, -232.25) * mm, "radius": 1 * mm});
            skCircle(sketch, "E151", {"center": v(171.06, -217.25) * mm, "radius": 1 * mm});
            skPoint(sketch, "E151.centerSnap0", {"position": v(171.06, -212.25) * mm});
            skCircle(sketch, "E152", {"center": v(171.06, -232.25) * mm, "radius": 1 * mm});
            skCircle(sketch, "E153", {"center": v(160.8, -224.75) * mm, "radius": 6.1 * mm});
            skPoint(sketch, "E153.centerSnap0", {"position": v(153.06, -224.75) * mm});
            skCircle(sketch, "E154", {"center": v(36.3, -184.25) * mm, "radius": 1 * mm});
            skCircle(sketch, "E155", {"center": v(44.8, -191.75) * mm, "radius": 6.1 * mm});
            skPoint(sketch, "E155.centerSnap0", {"position": v(38.8, -191.75) * mm});
            skPoint(sketch, "E155.centerSnap1", {"position": v(44.8, -185.75) * mm});
            skCircle(sketch, "E156", {"center": v(160.8, -250.75) * mm, "radius": 6.1 * mm});
            skPoint(sketch, "E156.centerSnap0", {"position": v(160.8, -244.75) * mm});
            skPoint(sketch, "E156.centerSnap1", {"position": v(154.8, -250.75) * mm});
            skCircle(sketch, "E157", {"center": v(132.3, -191.75) * mm, "radius": 6.1 * mm});
            skPoint(sketch, "E157.centerSnap0", {"position": v(126.3, -191.75) * mm});
            skPoint(sketch, "E157.centerSnap1", {"position": v(132.3, -185.75) * mm});
            skCircle(sketch, "E158", {"center": v(-0.2, -148.75) * mm, "radius": 1.5 * mm});
            skCircle(sketch, "E159", {"center": v(-0.2, -171.75) * mm, "radius": 1.5 * mm});
            skCircle(sketch, "E160", {"center": v(177.3, -208.75) * mm, "radius": 1.5 * mm});
            skCircle(sketch, "E161", {"center": v(177.3, -228.75) * mm, "radius": 1.5 * mm});
            skCircle(sketch, "E162", {"center": v(177.3, -248.75) * mm, "radius": 1.5 * mm});
            skCircle(sketch, "E163", {"center": v(177.3, -168.75) * mm, "radius": 1.5 * mm});
            skCircle(sketch, "E164", {"center": v(177.3, -188.75) * mm, "radius": 1.5 * mm});
            skCircle(sketch, "E165", {"center": v(177.3, -148.75) * mm, "radius": 1.5 * mm});
            skCircle(sketch, "E166", {"center": v(36.3, -199.25) * mm, "radius": 1 * mm});
            skCircle(sketch, "E167", {"center": v(53.3, -184.25) * mm, "radius": 1 * mm});
            skCircle(sketch, "E168", {"center": v(53.3, -199.25) * mm, "radius": 1 * mm});
            skCircle(sketch, "E169", {"center": v(123.8, -184.25) * mm, "radius": 1 * mm});
            skCircle(sketch, "E170", {"center": v(123.8, -199.25) * mm, "radius": 1 * mm});
            skCircle(sketch, "E171", {"center": v(140.8, -184.25) * mm, "radius": 1 * mm});
            skCircle(sketch, "E172", {"center": v(140.8, -199.25) * mm, "radius": 1 * mm});
            skCircle(sketch, "E173", {"center": v(152.3, -244.75) * mm, "radius": 1 * mm});
            skCircle(sketch, "E174", {"center": v(152.3, -256.75) * mm, "radius": 1 * mm});
            skCircle(sketch, "E175", {"center": v(169.3, -244.75) * mm, "radius": 1 * mm});
            skCircle(sketch, "E176", {"center": v(169.3, -256.75) * mm, "radius": 1 * mm});
            skCircle(sketch, "E177", {"center": v(88.56, -145.75) * mm, "radius": 1.1 * mm});
            skCircle(sketch, "E178", {"center": v(-0.2, -196.75) * mm, "radius": 1.5 * mm});
            skLineSegment(sketch, "E179.bottom", {"start": v(58.56, -140.75) * mm, "end": v(118.56, -140.75) * mm});
            skLineSegment(sketch, "E179.top", {"start": v(58.56, -133.75) * mm, "end": v(118.56, -133.75) * mm});
            skLineSegment(sketch, "E179.left", {"start": v(58.56, -140.75) * mm, "end": v(58.56, -133.75) * mm});
            skLineSegment(sketch, "E179.right", {"start": v(118.56, -140.75) * mm, "end": v(118.56, -133.75) * mm});
            skCircle(sketch, "E180", {"center": v(68.56, -137.25) * mm, "radius": 1.5 * mm});
            skCircle(sketch, "E181", {"center": v(108.56, -137.25) * mm, "radius": 1.5 * mm});
            skLineSegment(sketch, "E182", {"start": v(35.47, -191.75) * mm, "end": v(171.08, -191.75) * mm, "construction": true});
            skLineSegment(sketch, "E183.bottom", {"start": v(111.06, -224.97) * mm, "end": v(126.06, -224.97) * mm, "construction": true});
            skLineSegment(sketch, "E183.top", {"start": v(110.06, -239.97) * mm, "end": v(126.06, -239.97) * mm, "construction": true});
            skCircle(sketch, "E184", {"center": v(118.56, -232.47) * mm, "radius": 6.1 * mm});
            skPoint(sketch, "E184.centerSnap0", {"position": v(118.56, -224.97) * mm});
            skLineSegment(sketch, "E185.bottom", {"start": v(111.06, -224.97) * mm, "end": v(126.06, -224.97) * mm});
            skLineSegment(sketch, "E185.top", {"start": v(111.06, -239.97) * mm, "end": v(126.06, -239.97) * mm});
            skLineSegment(sketch, "E185.left", {"start": v(111.06, -224.97) * mm, "end": v(111.06, -239.97) * mm, "construction": true});
            skLineSegment(sketch, "E185.right", {"start": v(126.06, -224.97) * mm, "end": v(126.06, -239.97) * mm});
            skCircle(sketch, "E186", {"center": v(86.56, -228.25) * mm, "radius": 12.5 * mm, "construction": true});
            skSolve(sketch);
        }
        {
            var Q0;
            Q0=makeQuery(id+"F4.imprint","IMPRINT",FACE,{"disambiguationData":[TD([[makeQuery(id+"F4.imprint","IMPRINT",EDGE,{"derivedFrom":sQuery(id+"F4.wireOp",EDGE,"E53.bottom")}),-1.0]])]});
            var Q1;
            Q1=makeQuery(id+"F4.imprint","IMPRINT",FACE,{"disambiguationData":[TD([[makeQuery(id+"F4.imprint","IMPRINT",EDGE,{"derivedFrom":sQuery(id+"F4.wireOp",EDGE,"E55.bottom")}),1.0]])]});
            var Q2;
            Q2=makeQuery(id+"F4.imprint","IMPRINT",FACE,{"disambiguationData":[TD([[makeQuery(id+"F4.imprint","IMPRINT",EDGE,{"derivedFrom":sQuery(id+"F4.wireOp",EDGE,"E54.bottom")}),-1.0]])]});
            extrude(context, id + "F5", {"entities" : qUnion([Q0, Q1, Q2]), "oppositeDirection" : true, "depth" : 3 * mm});
        }
        {
            var Q0;
            Q0=qSketchRegion(id+"F4",true);
            extrude(context, id + "F6", {"entities" : qUnion([Q0]), "operationType" : NewBodyOperationType.ADD, "depth" : 2 * mm});
        }
        {
            var Q0;
            Q0=makeQuery(id+"F4.imprint","IMPRINT",FACE,{"disambiguationData":[TD([[makeQuery(id+"F4.imprint","IMPRINT",EDGE,{"derivedFrom":sQuery(id+"F4.wireOp",EDGE,"E50.bottom")}),-1.0]])]});
            var sketch = newSketch(context, id + "F7", { "sketchPlane" : qUnion([Q0])});
            skLineSegment(sketch, "E187.bottom", {"start": v(182.06, -174.75) * mm, "end": v(118.56, -174.75) * mm});
            skLineSegment(sketch, "E187.top", {"start": v(182.06, -175.75) * mm, "end": v(118.56, -175.75) * mm});
            skLineSegment(sketch, "E187.left", {"start": v(182.06, -174.75) * mm, "end": v(182.06, -175.75) * mm});
            skLineSegment(sketch, "E187.right", {"start": v(-4.94, -174.75) * mm, "end": v(-4.94, -175.75) * mm});
            skLineSegment(sketch, "E188.bottom", {"start": v(104.28, -208.97) * mm, "end": v(33.28, -208.97) * mm});
            skLineSegment(sketch, "E188.top", {"start": v(104.28, -209.97) * mm, "end": v(33.28, -209.97) * mm});
            skLineSegment(sketch, "E188.left", {"start": v(104.28, -208.97) * mm, "end": v(104.28, -209.97) * mm});
            skLineSegment(sketch, "E188.right", {"start": v(33.28, -208.97) * mm, "end": v(33.28, -209.97) * mm});
            skLineSegment(sketch, "E189.bottom", {"start": v(104.28, -209.97) * mm, "end": v(103.28, -209.97) * mm});
            skLineSegment(sketch, "E189.top", {"start": v(104.28, -244.97) * mm, "end": v(103.28, -244.97) * mm});
            skLineSegment(sketch, "E189.left", {"start": v(104.28, -209.97) * mm, "end": v(104.28, -244.97) * mm});
            skLineSegment(sketch, "E189.right", {"start": v(103.28, -209.97) * mm, "end": v(103.28, -244.97) * mm});
            skLineSegment(sketch, "E190.bottom", {"start": v(89.06, -148.97) * mm, "end": v(88.06, -148.97) * mm});
            skLineSegment(sketch, "E190.top", {"start": v(89.06, -208.97) * mm, "end": v(88.06, -208.97) * mm});
            skLineSegment(sketch, "E190.left", {"start": v(89.06, -148.97) * mm, "end": v(89.06, -174.75) * mm});
            skLineSegment(sketch, "E190.right", {"start": v(88.06, -148.97) * mm, "end": v(88.06, -174.75) * mm});
            skLineSegment(sketch, "E191.bottom", {"start": v(59.56, -140.75) * mm, "end": v(58.56, -140.75) * mm});
            skLineSegment(sketch, "E191.top", {"start": v(59.56, -208.97) * mm, "end": v(58.56, -208.97) * mm});
            skLineSegment(sketch, "E191.left", {"start": v(59.56, -140.75) * mm, "end": v(59.56, -174.75) * mm});
            skLineSegment(sketch, "E191.right", {"start": v(58.56, -140.75) * mm, "end": v(58.56, -174.75) * mm});
            skLineSegment(sketch, "E192.bottom", {"start": v(147.06, -140.75) * mm, "end": v(146.06, -140.75) * mm});
            skLineSegment(sketch, "E192.top", {"start": v(147.06, -263.97) * mm, "end": v(146.06, -263.97) * mm});
            skLineSegment(sketch, "E192.left", {"start": v(147.06, -140.75) * mm, "end": v(147.06, -263.97) * mm});
            skLineSegment(sketch, "E192.right", {"start": v(146.06, -140.75) * mm, "end": v(146.06, -263.97) * mm});
            skLineSegment(sketch, "E193.bottom", {"start": v(30.06, -140.75) * mm, "end": v(31.06, -140.75) * mm});
            skLineSegment(sketch, "E193.top", {"start": v(30.06, -208.97) * mm, "end": v(31.06, -208.97) * mm});
            skLineSegment(sketch, "E193.left", {"start": v(30.06, -140.75) * mm, "end": v(30.06, -208.97) * mm});
            skLineSegment(sketch, "E193.right", {"start": v(31.06, -140.75) * mm, "end": v(31.06, -208.97) * mm});
            skLineSegment(sketch, "E194.bottom", {"start": v(117.56, -140.75) * mm, "end": v(118.56, -140.75) * mm});
            skLineSegment(sketch, "E194.top", {"start": v(117.56, -208.97) * mm, "end": v(118.56, -208.97) * mm});
            skLineSegment(sketch, "E194.left", {"start": v(117.56, -140.75) * mm, "end": v(117.56, -174.75) * mm});
            skLineSegment(sketch, "E194.right", {"start": v(118.56, -140.75) * mm, "end": v(118.56, -174.75) * mm});
            skLineSegment(sketch, "E195.bottom", {"start": v(104.28, -244.97) * mm, "end": v(33.28, -244.97) * mm});
            skLineSegment(sketch, "E195.top", {"start": v(104.28, -245.97) * mm, "end": v(33.28, -245.97) * mm});
            skLineSegment(sketch, "E195.left", {"start": v(104.28, -244.97) * mm, "end": v(104.28, -245.97) * mm});
            skLineSegment(sketch, "E195.right", {"start": v(33.28, -244.97) * mm, "end": v(33.28, -245.97) * mm});
            skLineSegment(sketch, "E196.top", {"start": v(59.56, -263.97) * mm, "end": v(58.56, -263.97) * mm});
            skLineSegment(sketch, "E196.left", {"start": v(59.56, -208.97) * mm, "end": v(59.56, -263.97) * mm});
            skLineSegment(sketch, "E196.right", {"start": v(58.56, -208.97) * mm, "end": v(58.56, -263.97) * mm});
            skLineSegment(sketch, "E197.bottom", {"start": v(89.06, -245.97) * mm, "end": v(88.06, -245.97) * mm});
            skLineSegment(sketch, "E197.top", {"start": v(89.06, -263.97) * mm, "end": v(88.06, -263.97) * mm});
            skLineSegment(sketch, "E197.left", {"start": v(89.06, -245.97) * mm, "end": v(89.06, -263.97) * mm});
            skLineSegment(sketch, "E197.right", {"start": v(88.06, -245.97) * mm, "end": v(88.06, -263.97) * mm});
            skLineSegment(sketch, "E198.bottom", {"start": v(147.06, -240.38) * mm, "end": v(182.06, -240.38) * mm});
            skLineSegment(sketch, "E198.top", {"start": v(147.06, -239.38) * mm, "end": v(182.06, -239.38) * mm});
            skLineSegment(sketch, "E198.left", {"start": v(147.06, -240.38) * mm, "end": v(147.06, -239.38) * mm});
            skLineSegment(sketch, "E198.right", {"start": v(182.06, -240.38) * mm, "end": v(182.06, -239.38) * mm});
            skLineSegment(sketch, "E199.bottom", {"start": v(182.06, -140.75) * mm, "end": v(-4.94, -140.75) * mm});
            skLineSegment(sketch, "E199.top", {"start": v(182.06, -141.75) * mm, "end": v(-4.94, -141.75) * mm});
            skLineSegment(sketch, "E199.left", {"start": v(182.06, -140.75) * mm, "end": v(182.06, -141.75) * mm});
            skLineSegment(sketch, "E199.right", {"start": v(-4.94, -140.75) * mm, "end": v(-4.94, -141.75) * mm});
            skLineSegment(sketch, "E200.trimOffspring", {"start": v(58.56, -175.75) * mm, "end": v(58.56, -208.97) * mm});
            skLineSegment(sketch, "E201.trimOffspring", {"start": v(59.56, -175.75) * mm, "end": v(59.56, -208.97) * mm});
            skLineSegment(sketch, "E202.trimOffspring", {"start": v(58.56, -175.75) * mm, "end": v(-4.94, -175.75) * mm});
            skLineSegment(sketch, "E203.trimOffspring", {"start": v(58.56, -174.75) * mm, "end": v(-4.94, -174.75) * mm});
            skLineSegment(sketch, "E204.trimOffspring", {"start": v(117.56, -175.75) * mm, "end": v(117.56, -208.97) * mm});
            skLineSegment(sketch, "E205.trimOffspring", {"start": v(118.56, -175.75) * mm, "end": v(118.56, -208.97) * mm});
            skLineSegment(sketch, "E206.trimOffspring", {"start": v(117.56, -175.75) * mm, "end": v(89.06, -175.75) * mm});
            skLineSegment(sketch, "E207.trimOffspring", {"start": v(117.56, -174.75) * mm, "end": v(89.06, -174.75) * mm});
            skLineSegment(sketch, "E208.trimOffspring", {"start": v(88.06, -175.75) * mm, "end": v(88.06, -208.97) * mm});
            skLineSegment(sketch, "E209.trimOffspring", {"start": v(88.06, -175.75) * mm, "end": v(59.56, -175.75) * mm});
            skLineSegment(sketch, "E210.trimOffspring", {"start": v(88.06, -174.75) * mm, "end": v(59.56, -174.75) * mm});
            skLineSegment(sketch, "E211.trimOffspring", {"start": v(89.06, -175.75) * mm, "end": v(89.06, -208.97) * mm});
            skLineSegment(sketch, "E212.bottom", {"start": v(104.28, -208.97) * mm, "end": v(146.06, -208.97) * mm});
            skLineSegment(sketch, "E212.top", {"start": v(104.28, -209.97) * mm, "end": v(146.06, -209.97) * mm});
            skLineSegment(sketch, "E212.right", {"start": v(146.06, -208.97) * mm, "end": v(146.06, -209.97) * mm});
            skSolve(sketch);
        }
        {
            var Q0;
            Q0=makeQuery(id+"F6.opExtrude","CAP_FACE",FACE,{"disambiguationData":[OSD([sQuery(id+"F4.wireOp",EDGE,"E50.bottom"),sQuery(id+"F4.wireOp",EDGE,"E50.top"),sQuery(id+"F4.wireOp",EDGE,"E50.left"),sQuery(id+"F4.wireOp",EDGE,"E50.right"),sQuery(id+"F4.wireOp",EDGE,"E51"),sQuery(id+"F4.wireOp",EDGE,"E52"),sQuery(id+"F4.wireOp",EDGE,"E67"),sQuery(id+"F4.wireOp",EDGE,"E68"),sQuery(id+"F4.wireOp",EDGE,"E69"),sQuery(id+"F4.wireOp",EDGE,"E70"),sQuery(id+"F4.wireOp",EDGE,"E71"),sQuery(id+"F4.wireOp",EDGE,"E72"),sQuery(id+"F4.wireOp",EDGE,"E73"),sQuery(id+"F4.wireOp",EDGE,"E74"),sQuery(id+"F4.wireOp",EDGE,"E75"),sQuery(id+"F4.wireOp",EDGE,"E83"),sQuery(id+"F4.wireOp",EDGE,"E84"),sQuery(id+"F4.wireOp",EDGE,"E85"),sQuery(id+"F4.wireOp",EDGE,"E86"),sQuery(id+"F4.wireOp",EDGE,"E87"),sQuery(id+"F4.wireOp",EDGE,"E104"),sQuery(id+"F4.wireOp",EDGE,"E105"),sQuery(id+"F4.wireOp",EDGE,"E106"),sQuery(id+"F4.wireOp",EDGE,"E107"),sQuery(id+"F4.wireOp",EDGE,"E108"),sQuery(id+"F4.wireOp",EDGE,"E109"),sQuery(id+"F4.wireOp",EDGE,"E110"),sQuery(id+"F4.wireOp",EDGE,"E111"),sQuery(id+"F4.wireOp",EDGE,"E112"),sQuery(id+"F4.wireOp",EDGE,"E113"),sQuery(id+"F4.wireOp",EDGE,"E116"),sQuery(id+"F4.wireOp",EDGE,"E118"),sQuery(id+"F4.wireOp",EDGE,"E119"),sQuery(id+"F4.wireOp",EDGE,"E120"),sQuery(id+"F4.wireOp",EDGE,"E121"),sQuery(id+"F4.wireOp",EDGE,"E122"),sQuery(id+"F4.wireOp",EDGE,"E123"),sQuery(id+"F4.wireOp",EDGE,"E124"),sQuery(id+"F4.wireOp",EDGE,"E125"),sQuery(id+"F4.wireOp",EDGE,"E126"),sQuery(id+"F4.wireOp",EDGE,"E127"),sQuery(id+"F4.wireOp",EDGE,"E128"),sQuery(id+"F4.wireOp",EDGE,"E129"),sQuery(id+"F4.wireOp",EDGE,"E130"),sQuery(id+"F4.wireOp",EDGE,"E131"),sQuery(id+"F4.wireOp",EDGE,"E132"),sQuery(id+"F4.wireOp",EDGE,"E133"),sQuery(id+"F4.wireOp",EDGE,"E134"),sQuery(id+"F4.wireOp",EDGE,"E135"),sQuery(id+"F4.wireOp",EDGE,"E136"),sQuery(id+"F4.wireOp",EDGE,"E137"),sQuery(id+"F4.wireOp",EDGE,"E138"),sQuery(id+"F4.wireOp",EDGE,"E139"),sQuery(id+"F4.wireOp",EDGE,"E140"),sQuery(id+"F4.wireOp",EDGE,"E141"),sQuery(id+"F4.wireOp",EDGE,"E142"),sQuery(id+"F4.wireOp",EDGE,"E143"),sQuery(id+"F4.wireOp",EDGE,"E144"),sQuery(id+"F4.wireOp",EDGE,"E145"),sQuery(id+"F4.wireOp",EDGE,"E146"),sQuery(id+"F4.wireOp",EDGE,"E147"),sQuery(id+"F4.wireOp",EDGE,"E148"),sQuery(id+"F4.wireOp",EDGE,"E149"),sQuery(id+"F4.wireOp",EDGE,"E150"),sQuery(id+"F4.wireOp",EDGE,"E151"),sQuery(id+"F4.wireOp",EDGE,"E152"),sQuery(id+"F4.wireOp",EDGE,"E153"),sQuery(id+"F4.wireOp",EDGE,"E154"),sQuery(id+"F4.wireOp",EDGE,"E155"),sQuery(id+"F4.wireOp",EDGE,"E156"),sQuery(id+"F4.wireOp",EDGE,"E157"),sQuery(id+"F4.wireOp",EDGE,"E158"),sQuery(id+"F4.wireOp",EDGE,"OnnnS06f-s26S-AFDA-oTM6-wnMq7venfp2T"),sQuery(id+"F4.wireOp",EDGE,"V2efC4Jm-4NAF-VBiO-pQnY-etMWDclGv5un"),sQuery(id+"F4.wireOp",EDGE,"E159"),sQuery(id+"F4.wireOp",EDGE,"7M3HGg5D-aMQl-LYs1-MsCg-zVmLHFwYCo0C"),sQuery(id+"F4.wireOp",EDGE,"e6U4q213-1LtL-vwCs-wLTg-mGHH5etSdpE2"),sQuery(id+"F4.wireOp",EDGE,"E160"),sQuery(id+"F4.wireOp",EDGE,"E161"),sQuery(id+"F4.wireOp",EDGE,"E162"),sQuery(id+"F4.wireOp",EDGE,"E163"),sQuery(id+"F4.wireOp",EDGE,"R6Wk8btU-zCGi-4TmP-5Jjd-FV93XaIFImrj"),sQuery(id+"F4.wireOp",EDGE,"E164"),sQuery(id+"F4.wireOp",EDGE,"E165"),sQuery(id+"F4.wireOp",EDGE,"E166"),sQuery(id+"F4.wireOp",EDGE,"E167"),sQuery(id+"F4.wireOp",EDGE,"E168"),sQuery(id+"F4.wireOp",EDGE,"E169"),sQuery(id+"F4.wireOp",EDGE,"E170"),sQuery(id+"F4.wireOp",EDGE,"E171"),sQuery(id+"F4.wireOp",EDGE,"E172"),sQuery(id+"F4.wireOp",EDGE,"E173"),sQuery(id+"F4.wireOp",EDGE,"E174"),sQuery(id+"F4.wireOp",EDGE,"E175"),sQuery(id+"F4.wireOp",EDGE,"E176"),sQuery(id+"F4.wireOp",EDGE,"2CZ2vCPZ-g25f-Aix0-Xy3j-dVw2FXJ3BshQ.bottom"),sQuery(id+"F4.wireOp",EDGE,"2CZ2vCPZ-g25f-Aix0-Xy3j-dVw2FXJ3BshQ.left"),sQuery(id+"F4.wireOp",EDGE,"2CZ2vCPZ-g25f-Aix0-Xy3j-dVw2FXJ3BshQ.right"),sQuery(id+"F4.wireOp",EDGE,"3PAsEz4y-MCME-JD8k-KRcV-DaMAZ5aYk3wh"),sQuery(id+"F4.wireOp",EDGE,"E177")])],"isStart":false});
            var sketch = newSketch(context, id + "F8", { "sketchPlane" : qUnion([Q0])});
            skLineSegment(sketch, "E213.bottom", {"start": v(-4.94, -140.75) * mm, "end": v(-5.94, -140.75) * mm});
            skLineSegment(sketch, "E213.top", {"start": v(-4.94, -208.97) * mm, "end": v(-5.94, -208.97) * mm});
            skLineSegment(sketch, "E213.left", {"start": v(-4.94, -140.75) * mm, "end": v(-4.94, -208.97) * mm});
            skLineSegment(sketch, "E213.right", {"start": v(-5.94, -140.75) * mm, "end": v(-5.94, -208.97) * mm});
            skLineSegment(sketch, "E214.bottom", {"start": v(-5.94, -208.97) * mm, "end": v(33.28, -208.97) * mm});
            skLineSegment(sketch, "E214.top", {"start": v(-5.94, -211.97) * mm, "end": v(33.28, -211.97) * mm});
            skLineSegment(sketch, "E214.left", {"start": v(-5.94, -208.97) * mm, "end": v(-5.94, -211.97) * mm});
            skLineSegment(sketch, "E214.right", {"start": v(33.28, -208.97) * mm, "end": v(33.28, -211.97) * mm});
            skLineSegment(sketch, "E215.bottom", {"start": v(33.28, -263.97) * mm, "end": v(30.28, -263.97) * mm});
            skLineSegment(sketch, "E215.top", {"start": v(33.28, -211.97) * mm, "end": v(30.28, -211.97) * mm});
            skLineSegment(sketch, "E215.left", {"start": v(33.28, -263.97) * mm, "end": v(33.28, -211.97) * mm});
            skLineSegment(sketch, "E215.right", {"start": v(30.28, -263.97) * mm, "end": v(30.28, -211.97) * mm});
            skLineSegment(sketch, "E216.bottom", {"start": v(182.06, -140.75) * mm, "end": v(183.06, -140.75) * mm});
            skLineSegment(sketch, "E216.top", {"start": v(182.06, -263.97) * mm, "end": v(183.06, -263.97) * mm});
            skLineSegment(sketch, "E216.left", {"start": v(182.06, -140.75) * mm, "end": v(182.06, -263.97) * mm});
            skLineSegment(sketch, "E216.right", {"start": v(183.06, -140.75) * mm, "end": v(183.06, -263.97) * mm});
            skLineSegment(sketch, "E217.bottom", {"start": v(183.06, -263.97) * mm, "end": v(169.06, -263.97) * mm});
            skLineSegment(sketch, "E217.top", {"start": v(183.06, -266.97) * mm, "end": v(169.06, -266.97) * mm});
            skLineSegment(sketch, "E217.left", {"start": v(183.06, -263.97) * mm, "end": v(183.06, -266.97) * mm});
            skLineSegment(sketch, "E217.right", {"start": v(169.06, -263.97) * mm, "end": v(169.06, -266.97) * mm});
            skLineSegment(sketch, "E218.bottom", {"start": v(153.56, -263.97) * mm, "end": v(118.56, -263.97) * mm});
            skLineSegment(sketch, "E218.top", {"start": v(153.56, -266.97) * mm, "end": v(118.56, -266.97) * mm});
            skLineSegment(sketch, "E218.left", {"start": v(153.56, -263.97) * mm, "end": v(153.56, -266.97) * mm});
            skLineSegment(sketch, "E218.right", {"start": v(118.56, -263.97) * mm, "end": v(118.56, -266.97) * mm});
            skLineSegment(sketch, "E219.bottom", {"start": v(30.28, -263.97) * mm, "end": v(102.28, -263.97) * mm});
            skLineSegment(sketch, "E219.top", {"start": v(30.28, -266.97) * mm, "end": v(102.28, -266.97) * mm});
            skLineSegment(sketch, "E219.left", {"start": v(30.28, -263.97) * mm, "end": v(30.28, -266.97) * mm});
            skLineSegment(sketch, "E219.right", {"start": v(102.28, -263.97) * mm, "end": v(102.28, -266.97) * mm});
            skLineSegment(sketch, "E220.bottom", {"start": v(118.56, -133.75) * mm, "end": v(119.56, -133.75) * mm});
            skLineSegment(sketch, "E220.top", {"start": v(118.56, -140.75) * mm, "end": v(119.56, -140.75) * mm});
            skLineSegment(sketch, "E220.left", {"start": v(118.56, -133.75) * mm, "end": v(118.56, -140.75) * mm});
            skLineSegment(sketch, "E220.right", {"start": v(119.56, -133.75) * mm, "end": v(119.56, -140.75) * mm});
            skLineSegment(sketch, "E221.bottom", {"start": v(119.56, -140.75) * mm, "end": v(125.56, -140.75) * mm});
            skLineSegment(sketch, "E221.top", {"start": v(119.56, -139.75) * mm, "end": v(125.56, -139.75) * mm});
            skLineSegment(sketch, "E221.left", {"start": v(119.56, -140.75) * mm, "end": v(119.56, -139.75) * mm});
            skLineSegment(sketch, "E221.right", {"start": v(125.56, -140.75) * mm, "end": v(125.56, -139.75) * mm});
            skLineSegment(sketch, "E222.bottom", {"start": v(58.56, -133.75) * mm, "end": v(57.56, -133.75) * mm});
            skLineSegment(sketch, "E222.top", {"start": v(58.56, -140.75) * mm, "end": v(57.56, -140.75) * mm});
            skLineSegment(sketch, "E222.left", {"start": v(58.56, -133.75) * mm, "end": v(58.56, -140.75) * mm});
            skLineSegment(sketch, "E222.right", {"start": v(57.56, -133.75) * mm, "end": v(57.56, -140.75) * mm});
            skLineSegment(sketch, "E223.bottom", {"start": v(57.56, -140.75) * mm, "end": v(51.56, -140.75) * mm});
            skLineSegment(sketch, "E223.top", {"start": v(57.56, -139.75) * mm, "end": v(51.56, -139.75) * mm});
            skLineSegment(sketch, "E223.left", {"start": v(57.56, -140.75) * mm, "end": v(57.56, -139.75) * mm});
            skLineSegment(sketch, "E223.right", {"start": v(51.56, -140.75) * mm, "end": v(51.56, -139.75) * mm});
            skSolve(sketch);
        }
        {
            var Q0;
            Q0=qSketchRegion(id+"F8",true);
            extrude(context, id + "F9", {"entities" : qUnion([Q0]), "operationType" : NewBodyOperationType.ADD, "oppositeDirection" : true, "depth" : 6 * mm});
        }
        {
            var Q0;
            Q0=qSketchRegion(id+"F7",true);
            extrude(context, id + "F10", {"entities" : qUnion([Q0]), "operationType" : NewBodyOperationType.ADD, "oppositeDirection" : true, "depth" : 4 * mm});
        }
        {
            var Q0;
            Q0=makeQuery(id+"F9.opExtrude","SWEPT_EDGE",EDGE,{"disambiguationData":[OSD([sQuery(id+"F8.wireOp",EDGE,"E214.top"),sQuery(id+"F8.wireOp",EDGE,"E214.left")])]});
            var Q1;
            Q1=makeQuery(id+"F9.opExtrude","SWEPT_EDGE",EDGE,{"disambiguationData":[OSD([sQuery(id+"F8.wireOp",EDGE,"E214.top"),sQuery(id+"F8.wireOp",EDGE,"E215.top"),sQuery(id+"F8.wireOp",EDGE,"E215.right")])]});
            var Q2;
            Q2=makeQuery(id+"F9.opExtrude","SWEPT_EDGE",EDGE,{"disambiguationData":[OSD([sQuery(id+"F8.wireOp",EDGE,"E219.top"),sQuery(id+"F8.wireOp",EDGE,"E219.left")])]});
            var Q3;
            Q3=makeQuery(id+"F9.opExtrude","SWEPT_EDGE",EDGE,{"disambiguationData":[OSD([sQuery(id+"F8.wireOp",EDGE,"E217.top"),sQuery(id+"F8.wireOp",EDGE,"E217.left")])]});
            fillet(context, id + "F11", {"entities" : qUnion([Q0, Q1, Q2, Q3]), "radius" : 2 * mm, "tangentPropagation" : true, "allowEdgeOverflow" : false});
        }
        {
            var Q0;
            {var subQ0=sQuery(id+"F4.wireOp",EDGE,"E180");var subQ1=sQuery(id+"F4.wireOp",EDGE,"E181");var subQ2=sQuery(id+"F4.wireOp",EDGE,"E179.top");Q0=makeQuery(id+"F10.boolean.opBoolean","SPLIT",FACE,{"disambiguationData":[TD([makeQuery(id+"F6.opExtrude","SWEPT_FACE",FACE,{"disambiguationData":[OSD([subQ2])]})])],"derivedFrom":makeQuery(id+"F6.opExtrude","CAP_FACE",FACE,{"disambiguationData":[OSD([sQuery(id+"F4.wireOp",EDGE,"E50.bottom"),sQuery(id+"F4.wireOp",EDGE,"E50.top"),sQuery(id+"F4.wireOp",EDGE,"E50.left"),sQuery(id+"F4.wireOp",EDGE,"E50.right"),sQuery(id+"F4.wireOp",EDGE,"E51"),sQuery(id+"F4.wireOp",EDGE,"E52"),sQuery(id+"F4.wireOp",EDGE,"E67"),sQuery(id+"F4.wireOp",EDGE,"E68"),sQuery(id+"F4.wireOp",EDGE,"E69"),sQuery(id+"F4.wireOp",EDGE,"E70"),sQuery(id+"F4.wireOp",EDGE,"E71"),sQuery(id+"F4.wireOp",EDGE,"E72"),sQuery(id+"F4.wireOp",EDGE,"E73"),sQuery(id+"F4.wireOp",EDGE,"E74"),sQuery(id+"F4.wireOp",EDGE,"E75"),sQuery(id+"F4.wireOp",EDGE,"E83"),sQuery(id+"F4.wireOp",EDGE,"E84"),sQuery(id+"F4.wireOp",EDGE,"E85"),sQuery(id+"F4.wireOp",EDGE,"E86"),sQuery(id+"F4.wireOp",EDGE,"E87"),sQuery(id+"F4.wireOp",EDGE,"E104"),sQuery(id+"F4.wireOp",EDGE,"E105"),sQuery(id+"F4.wireOp",EDGE,"E106"),sQuery(id+"F4.wireOp",EDGE,"E107"),sQuery(id+"F4.wireOp",EDGE,"E108"),sQuery(id+"F4.wireOp",EDGE,"E109"),sQuery(id+"F4.wireOp",EDGE,"E110"),sQuery(id+"F4.wireOp",EDGE,"E111"),sQuery(id+"F4.wireOp",EDGE,"E112"),sQuery(id+"F4.wireOp",EDGE,"E113"),sQuery(id+"F4.wireOp",EDGE,"E116"),sQuery(id+"F4.wireOp",EDGE,"E118"),sQuery(id+"F4.wireOp",EDGE,"E119"),sQuery(id+"F4.wireOp",EDGE,"E120"),sQuery(id+"F4.wireOp",EDGE,"E121"),sQuery(id+"F4.wireOp",EDGE,"E122"),sQuery(id+"F4.wireOp",EDGE,"E123"),sQuery(id+"F4.wireOp",EDGE,"E124"),sQuery(id+"F4.wireOp",EDGE,"E125"),sQuery(id+"F4.wireOp",EDGE,"E126"),sQuery(id+"F4.wireOp",EDGE,"E127"),sQuery(id+"F4.wireOp",EDGE,"E128"),sQuery(id+"F4.wireOp",EDGE,"E129"),sQuery(id+"F4.wireOp",EDGE,"E130"),sQuery(id+"F4.wireOp",EDGE,"E131"),sQuery(id+"F4.wireOp",EDGE,"E132"),sQuery(id+"F4.wireOp",EDGE,"E133"),sQuery(id+"F4.wireOp",EDGE,"E134"),sQuery(id+"F4.wireOp",EDGE,"E135"),sQuery(id+"F4.wireOp",EDGE,"E136"),sQuery(id+"F4.wireOp",EDGE,"E137"),sQuery(id+"F4.wireOp",EDGE,"E138"),sQuery(id+"F4.wireOp",EDGE,"E139"),sQuery(id+"F4.wireOp",EDGE,"E140"),sQuery(id+"F4.wireOp",EDGE,"E141"),sQuery(id+"F4.wireOp",EDGE,"E142"),sQuery(id+"F4.wireOp",EDGE,"E143"),sQuery(id+"F4.wireOp",EDGE,"E144"),sQuery(id+"F4.wireOp",EDGE,"E145"),sQuery(id+"F4.wireOp",EDGE,"E146"),sQuery(id+"F4.wireOp",EDGE,"E147"),sQuery(id+"F4.wireOp",EDGE,"E148"),sQuery(id+"F4.wireOp",EDGE,"E149"),sQuery(id+"F4.wireOp",EDGE,"E150"),sQuery(id+"F4.wireOp",EDGE,"E151"),sQuery(id+"F4.wireOp",EDGE,"E152"),sQuery(id+"F4.wireOp",EDGE,"E153"),sQuery(id+"F4.wireOp",EDGE,"E154"),sQuery(id+"F4.wireOp",EDGE,"E155"),sQuery(id+"F4.wireOp",EDGE,"E156"),sQuery(id+"F4.wireOp",EDGE,"E157"),sQuery(id+"F4.wireOp",EDGE,"E158"),sQuery(id+"F4.wireOp",EDGE,"E159"),sQuery(id+"F4.wireOp",EDGE,"E160"),sQuery(id+"F4.wireOp",EDGE,"E161"),sQuery(id+"F4.wireOp",EDGE,"E162"),sQuery(id+"F4.wireOp",EDGE,"E163"),sQuery(id+"F4.wireOp",EDGE,"E164"),sQuery(id+"F4.wireOp",EDGE,"E165"),sQuery(id+"F4.wireOp",EDGE,"E166"),sQuery(id+"F4.wireOp",EDGE,"E167"),sQuery(id+"F4.wireOp",EDGE,"E168"),sQuery(id+"F4.wireOp",EDGE,"E169"),sQuery(id+"F4.wireOp",EDGE,"E170"),sQuery(id+"F4.wireOp",EDGE,"E171"),sQuery(id+"F4.wireOp",EDGE,"E172"),sQuery(id+"F4.wireOp",EDGE,"E173"),sQuery(id+"F4.wireOp",EDGE,"E174"),sQuery(id+"F4.wireOp",EDGE,"E175"),sQuery(id+"F4.wireOp",EDGE,"E176"),sQuery(id+"F4.wireOp",EDGE,"2CZ2vCPZ-g25f-Aix0-Xy3j-dVw2FXJ3BshQ.bottom"),sQuery(id+"F4.wireOp",EDGE,"2CZ2vCPZ-g25f-Aix0-Xy3j-dVw2FXJ3BshQ.left"),sQuery(id+"F4.wireOp",EDGE,"2CZ2vCPZ-g25f-Aix0-Xy3j-dVw2FXJ3BshQ.right"),sQuery(id+"F4.wireOp",EDGE,"3PAsEz4y-MCME-JD8k-KRcV-DaMAZ5aYk3wh"),sQuery(id+"F4.wireOp",EDGE,"E177"),sQuery(id+"F4.wireOp",EDGE,"E178"),subQ2,sQuery(id+"F4.wireOp",EDGE,"E179.left"),sQuery(id+"F4.wireOp",EDGE,"E179.right"),subQ0,subQ1])],"isStart":true})});}
            extrude(context, id + "F12", {"entities" : qUnion([Q0]), "operationType" : NewBodyOperationType.ADD, "depth" : 4 * mm});
        }
    });
